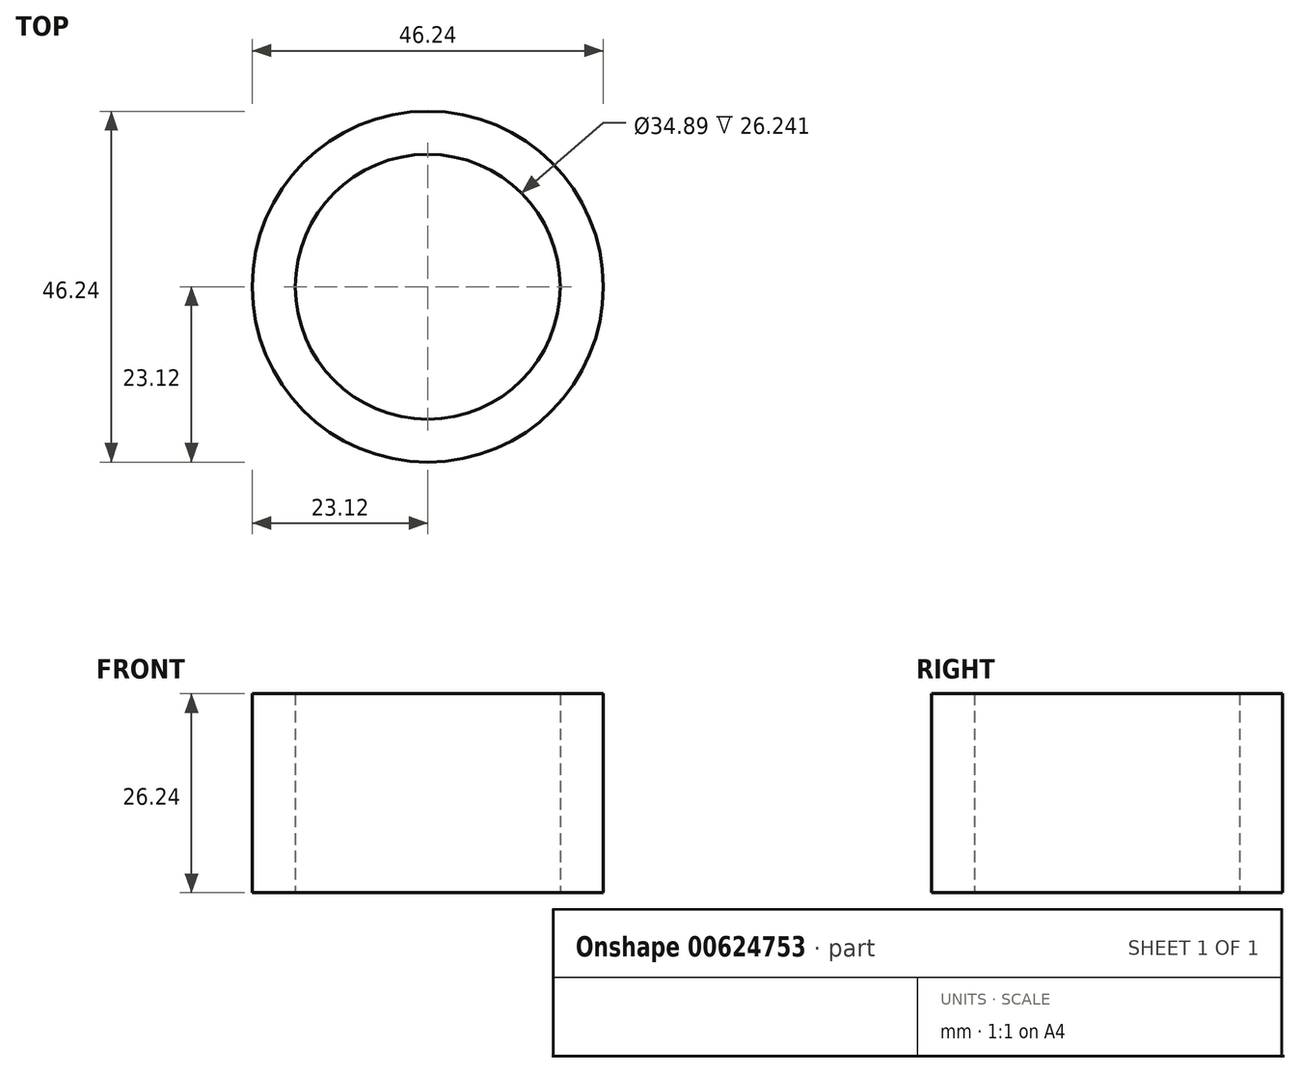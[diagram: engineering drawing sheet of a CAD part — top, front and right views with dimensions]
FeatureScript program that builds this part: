
annotation { "Feature Type Name" : "Feature", "Feature Type Description" : "" }
export const myFeature = defineFeature(function(context is Context, id is Id, definition is map)
    precondition{}
    {
        {
            var Q0;
            Q0=qCreatedBy(makeId("Right.planeOp"),FACE);
            var sketch = newSketch(context, id + "F0", { "sketchPlane" : qUnion([Q0])});
            skLineSegment(sketch, "E0.bottom", {"start": v(17.45, 26.24) * mm, "end": v(23.12, 26.24) * mm});
            skLineSegment(sketch, "E0.top", {"start": v(17.45, 0) * mm, "end": v(23.12, 0) * mm});
            skLineSegment(sketch, "E0.left", {"start": v(17.45, 26.24) * mm, "end": v(17.45, 0) * mm});
            skLineSegment(sketch, "E0.right", {"start": v(23.12, 26.24) * mm, "end": v(23.12, 0) * mm});
            skLineSegment(sketch, "E1", {"start": v(0, 0) * mm, "end": v(0, 39.08) * mm, "construction": true});
            skSolve(sketch);
        }
        {
            var Q0;
            Q0=makeQuery(id+"F0.imprint","IMPRINT",FACE,{"disambiguationData":[TD([[makeQuery(id+"F0.imprint","IMPRINT",EDGE,{"derivedFrom":sQuery(id+"F0.wireOp",EDGE,"E0.bottom")}),-1.0]])]});
            var Q1;
            Q1=sQuery(id+"F0.wireOp",EDGE,"E1");
            revolve(context, id + "F1", {"entities" : qUnion([Q0]), "axis" : qUnion([Q1]), "revolveType" : RevolveType.FULL});
        }
    });
